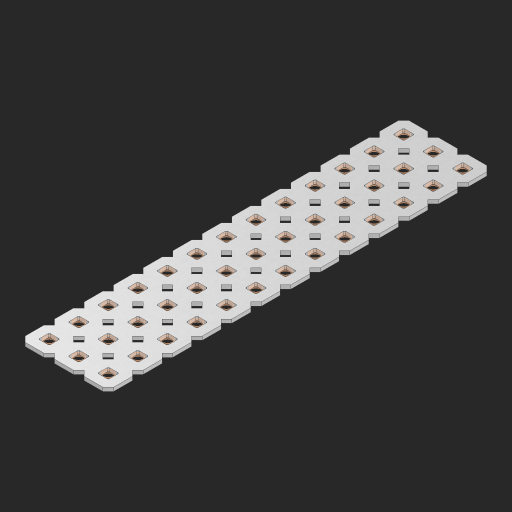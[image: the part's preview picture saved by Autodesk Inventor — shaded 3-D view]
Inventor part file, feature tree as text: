
AUTODESK INVENTOR PART (.ipt)
format: ipt  version: 2023 (Build 270158000, 158)  size: 654,848 bytes
history: native  units: in
note: dims shown in document units (in); Inventor stores cm internally (conversion verified against a paired STEP export)
features: other x40, extrude x38, sketch x2, pattern_linear x1
ambient origin geometry x8: Origin, YZ Plane, XZ Plane, XY Plane, X Axis, Y Axis, Z Axis, Center Point
bodies: Solid1 (feature_tree), Body (feature_tree)
feature tree (81):
  pattern_linear  "Rectangular Pattern1"  Spacing1=0.09in  [1 undecoded]
  sketch  "Sketch1"  dims[d1=0.5in]
  sketch  "Sketch2"  dims[d2=0.182in d3=0.09in d4=0.09in d5=0.09in d6=0.09in d7=0.09in d8=0.09in d9=0.09in d10=0.09in d11=0.02in d13=0.0in d14=0.172in d15=0.0625in d16=0.0in d19=0.5in d22=0.5in]
  other  "Srf1"
  other  "Srf126"
  other  "Srf127"
  other  "Srf128"
  other  "Srf129"
  other  "Srf130"
  other  "Srf131"
  other  "Srf250"
  other  "Srf251"
  other  "Srf252"
  other  "Srf253"
  other  "Srf254"
  other  "Srf255"
  other  "Srf268"
  other  "Srf269"
  other  "Srf270"
  other  "Srf271"
  other  "Srf272"
  other  "Srf273"
  other  "Srf274"
  other  "Srf275"
  other  "Srf276"
  other  "Srf277"
  other  "Srf278"
  other  "Srf279"
  other  "Srf280"
  other  "Srf293"
  other  "Srf294"
  other  "Srf295"
  other  "Srf296"
  other  "Srf297"
  other  "Srf298"
  other  "Srf299"
  other  "Srf300"
  other  "Srf301"
  other  "Srf302"
  other  "Srf303"
  other  "Srf304"
  other  "Srf305"
  other  "Circle"
  extrude  "ExtrusionSrf126"  Depth=0.09in
  extrude  "ExtrusionSrf127"  Depth=0.09in
  extrude  "ExtrusionSrf128"  Depth=0.09in
  extrude  "ExtrusionSrf129"  Depth=0.09in
  extrude  "ExtrusionSrf130"  Depth=0.09in
  extrude  "ExtrusionSrf131"  Depth=0.09in
  extrude  "ExtrusionSrf250"  Depth=0.09in
  extrude  "ExtrusionSrf251"  Depth=0.02in
  extrude  "ExtrusionSrf252"  TaperAngle=0.0deg  [1 undecoded]
  extrude  "ExtrusionSrf253"  Depth=0.5in
  extrude  "ExtrusionSrf254"  Depth=0.0625in TaperAngle=0.0deg
  extrude  "ExtrusionSrf255"  Depth=0.5in
  extrude  "ExtrusionSrf268"  Depth=0.5in
  extrude  "ExtrusionSrf269"  [1 undecoded]
  extrude  "ExtrusionSrf270"  [1 undecoded]
  extrude  "ExtrusionSrf271"  [1 undecoded]
  extrude  "ExtrusionSrf272"  [1 undecoded]
  extrude  "ExtrusionSrf273"  [1 undecoded]
  extrude  "ExtrusionSrf274"  [1 undecoded]
  extrude  "ExtrusionSrf275"  [1 undecoded]
  extrude  "ExtrusionSrf276"  [1 undecoded]
  extrude  "ExtrusionSrf277"  [1 undecoded]
  extrude  "ExtrusionSrf278"  [1 undecoded]
  extrude  "ExtrusionSrf279"  [1 undecoded]
  extrude  "ExtrusionSrf280"  [1 undecoded]
  extrude  "ExtrusionSrf293"  [1 undecoded]
  extrude  "ExtrusionSrf294"  [1 undecoded]
  extrude  "ExtrusionSrf295"  [1 undecoded]
  extrude  "ExtrusionSrf296"  [1 undecoded]
  extrude  "ExtrusionSrf297"  [1 undecoded]
  extrude  "ExtrusionSrf298"  [1 undecoded]
  extrude  "ExtrusionSrf299"  [1 undecoded]
  extrude  "ExtrusionSrf300"  [1 undecoded]
  extrude  "ExtrusionSrf301"  [1 undecoded]
  extrude  "ExtrusionSrf302"  [1 undecoded]
  extrude  "ExtrusionSrf303"  [1 undecoded]
  extrude  "ExtrusionSrf304"  [1 undecoded]
  extrude  "ExtrusionSrf305"  [1 undecoded]
note: 27 required parameter values undecoded (feature->parameter linkage not recoverable at this tier; creation-order binding heuristic only, values carry confidence <= 0.55)
